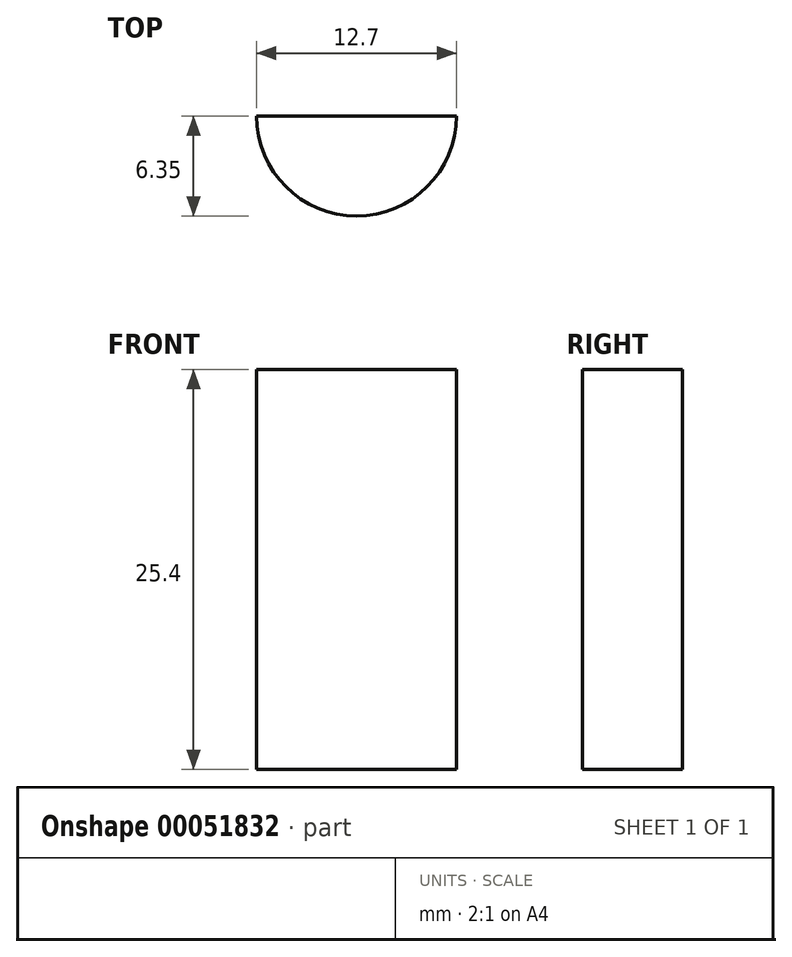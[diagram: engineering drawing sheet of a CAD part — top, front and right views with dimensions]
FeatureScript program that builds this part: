
annotation { "Feature Type Name" : "Feature", "Feature Type Description" : "" }
export const myFeature = defineFeature(function(context is Context, id is Id, definition is map)
    precondition{}
    {
        {
            var Q0;
            Q0=qCreatedBy(makeId("Top.planeOp"),FACE);
            var sketch = newSketch(context, id + "F0", { "sketchPlane" : qUnion([Q0])});
            skLineSegment(sketch, "E0", {"start": v(-6.35, 0) * mm, "end": v(6.35, 0) * mm});
            skArc(sketch, "E1", {"start": v(6.35, 0) * mm, "mid": v(0, -6.35) * mm, "end": v(-6.35, 0) * mm});
            skSolve(sketch);
        }
        {
            var Q0;
            Q0=makeQuery(id+"F0.imprint","IMPRINT",FACE,{"disambiguationData":[TD([[makeQuery(id+"F0.imprint","IMPRINT",EDGE,{"derivedFrom":sQuery(id+"F0.wireOp",EDGE,"E0")}),-1.0]])]});
            extrude(context, id + "F1", {"entities" : qUnion([Q0]), "depth" : 25.4 * mm});
        }
    });
